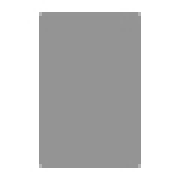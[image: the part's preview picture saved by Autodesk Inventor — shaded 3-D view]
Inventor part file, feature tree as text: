
AUTODESK INVENTOR PART (.ipt)
format: ipt  version: 2025 (Build 290162010, 162A)  size: 165,376 bytes
history: native  units: mm
features: sketch x5, reference x4, other x4, hole x3, extrude x2, fillet x2, chamfer x1
ambient origin geometry x8: Origin, YZ Plane, XZ Plane, XY Plane, X Axis, Y Axis, Z Axis, Center Point
bodies: Solid1 (feature_tree)
feature tree (21):
  extrude  "Extrusion1"  Depth=12.0mm
  fillet  "Fillet1"  Radius=200.0mm
  chamfer  "Chamfer1"  [1 undecoded]
  sketch  "Skizze2"  dims[d3=100.0mm]
  hole  "Bohrung1"  [1 undecoded]
  hole  "Bohrung2"  [1 undecoded]
  hole  "Bohrung3"  [1 undecoded]
  extrude  "Extrusion2"  Depth=3.0mm
  fillet  "Rundung2"  Radius=70.0mm
  sketch  "Sketch1"  dims[d0=24.0mm d1=12.0mm d2=200.0mm]
  sketch  "Skizze3"  dims[d4=8.0mm]
  sketch  "Skizze4"  dims[d5=0.0mm]
  reference  "Referenz1"
  reference  "Referenz2"
  reference  "Referenz3"
  reference  "Referenz4"
  sketch  "Skizze5"  dims[d6=0.0mm d7=0.0mm d8=0.0mm d9=2.0mm d10=45.0deg d11=0.0mm d12=15.0mm d13=70.0mm d14=5.3mm d15=6.0mm d16=15.0mm d17=1.0mm d18=90.0deg d19=8.0mm d20=20.594885mm d21=4.134mm d22=10.0mm d23=6.3mm d24=2.0mm d25=90.0deg d26=8.0mm d27=20.594885mm d28=2.459mm d29=5.0mm d30=4.0mm d31=2.0mm d32=90.0deg d33=8.0mm d34=20.594885mm d35=50.0mm d36=12.0mm d37=0.0mm d38=0.0mm d39=3.0mm]
  other  "<userpath>\GIT\HDVKBM\CAD\Krandemonstrator\Demonstrator.iam"
  other  "Demonstrator.iam"
  other  "MontageAufnahmeLO:2"
  other  "MontageAufnahmeLO-LH:2"
note: 4 required parameter values undecoded (feature->parameter linkage not recoverable at this tier; creation-order binding heuristic only, values carry confidence <= 0.55)
